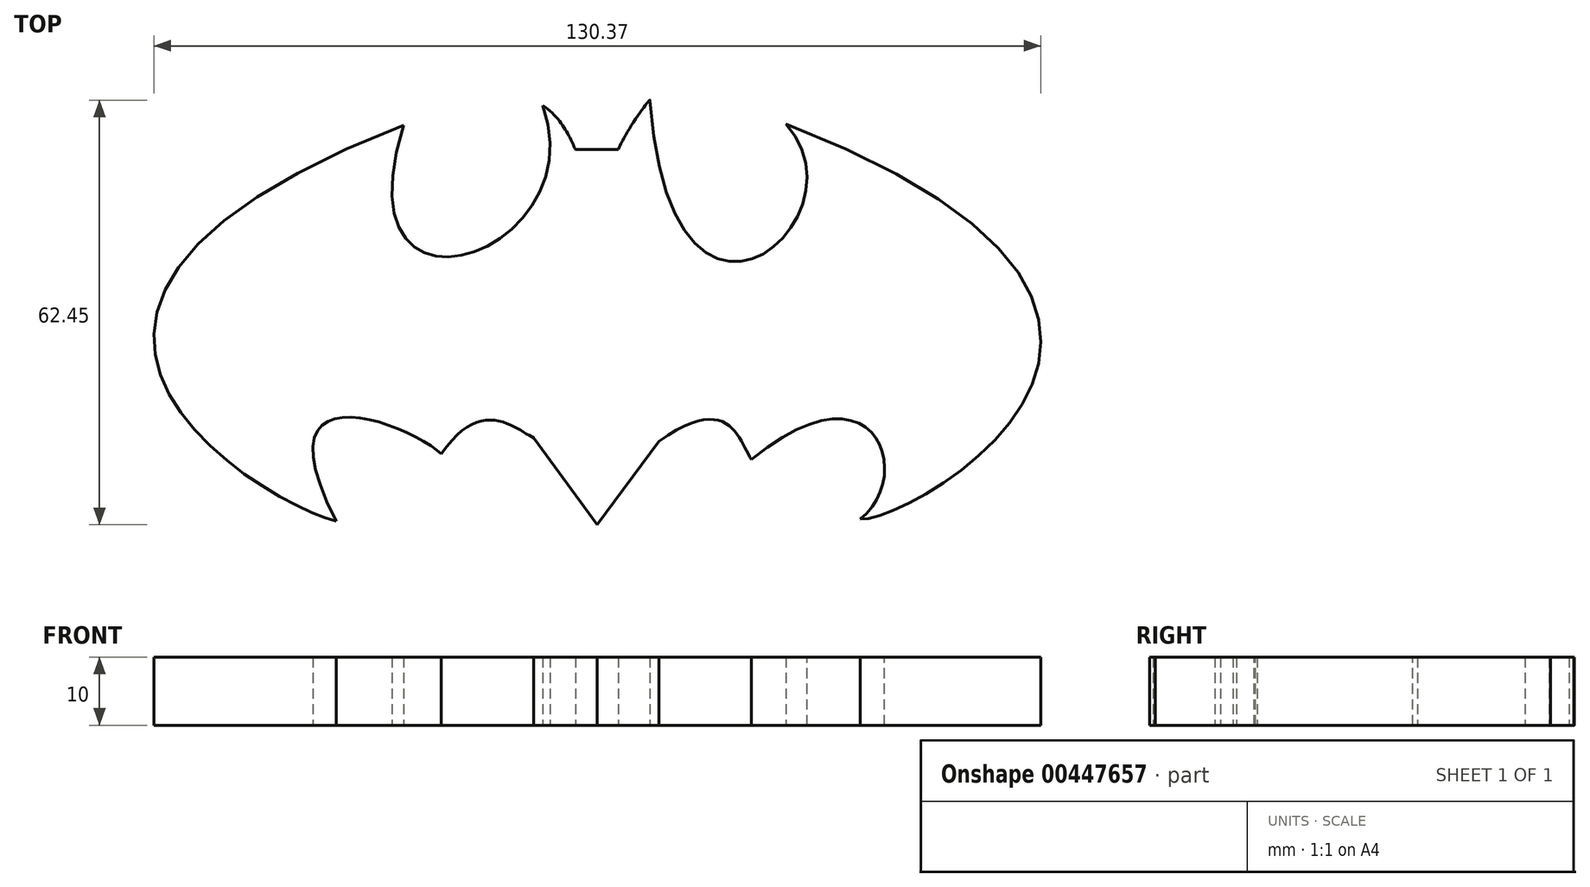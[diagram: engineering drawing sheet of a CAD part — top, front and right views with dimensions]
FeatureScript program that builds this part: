
annotation { "Feature Type Name" : "Feature", "Feature Type Description" : "" }
export const myFeature = defineFeature(function(context is Context, id is Id, definition is map)
    precondition{}
    {
        {
            var Q0;
            Q0=qCreatedBy(makeId("Top.planeOp"),FACE);
            var sketch = newSketch(context, id + "F0", { "sketchPlane" : qUnion([Q0])});
            skLineSegment(sketch, "E0", {"start": v(-3.2, 40.37) * mm, "end": v(3.2, 40.37) * mm});
            skLineSegment(sketch, "E1", {"start": v(0, -14.8) * mm, "end": v(-9.33, -2) * mm});
            skLineSegment(sketch, "E2", {"start": v(0, -14.8) * mm, "end": v(9.06, -2.53) * mm});
            skFitSpline(sketch, "E3", {"points": [v(-38.38, -14.26) * mm, v(-22.92, -4.4) * mm], "startDerivative": vector(-35.98, 69.56) * mm, "endDerivative": vector(13.6, -13.2) * mm});
            skFitSpline(sketch, "E4", {"points": [v(38.64, -14) * mm, v(22.65, -5.2) * mm], "startDerivative": vector(23.98, 18.39) * mm, "endDerivative": vector(-55.96, -45.57) * mm});
            skFitSpline(sketch, "E5", {"points": [v(22.65, -5.2) * mm, v(9.06, -2.53) * mm], "startDerivative": vector(-5.6, 8) * mm, "endDerivative": vector(-31.98, -22.39) * mm});
            skFitSpline(sketch, "E6", {"points": [v(27.72, 44.1) * mm, v(38.64, -14) * mm], "startDerivative": vector(219.06, -83.95) * mm, "endDerivative": vector(-21.59, 1.6) * mm});
            skFitSpline(sketch, "E7", {"points": [v(-28.48, 43.92) * mm, v(-38.38, -14.26) * mm], "startDerivative": vector(-208.78, -80.2) * mm, "endDerivative": vector(32.78, -8) * mm});
            skFitSpline(sketch, "E8", {"points": [v(-8.04, 46.87) * mm, v(-3.2, 40.37) * mm], "startDerivative": vector(8.93, -5.9) * mm, "endDerivative": vector(2.4, -4.8) * mm});
            skFitSpline(sketch, "E9", {"points": [v(4.8, 43.57) * mm, v(3.2, 40.37) * mm, v(7.73, 47.57) * mm, v(4.8, 43.57) * mm]});
            skPoint(sketch, "E10.startDerivative.orphan", {"position": v(0, 31.17) * mm});
            skFitSpline(sketch, "E11", {"points": [v(-8.04, 46.87) * mm, v(-28.48, 43.92) * mm], "startDerivative": vector(24.12, -65.87) * mm, "endDerivative": vector(30.5, 97) * mm});
            skFitSpline(sketch, "E12", {"points": [v(7.73, 47.57) * mm, v(27.72, 44.1) * mm], "startDerivative": vector(9.6, -128.72) * mm, "endDerivative": vector(-37.58, 40.77) * mm});
            skPoint(sketch, "E13.endDerivative.orphan", {"position": v(-18.92, 0) * mm});
            skPoint(sketch, "E13.startDerivative.orphan", {"position": v(-14.92, 0) * mm});
            skFitSpline(sketch, "E14", {"points": [v(-9.33, -2) * mm, v(-22.92, -4.4) * mm], "startDerivative": vector(-7.26, 2.94) * mm, "endDerivative": vector(-18, -26.68) * mm});
            skSolve(sketch);
        }
        {
            var Q0;
            Q0 = qSketchRegion(id + "F0", true);
            extrude(context, id + "F1", {"entities" : qUnion([Q0]), "depth" : 10 * mm});
        }
        {
            var Q0;
            Q0 = qSketchRegion(id + "F0", true);
            extrude(context, id + "F2", {"entities" : qUnion([Q0]), "operationType" : NewBodyOperationType.ADD, "depth" : 10 * mm});
        }
    });
